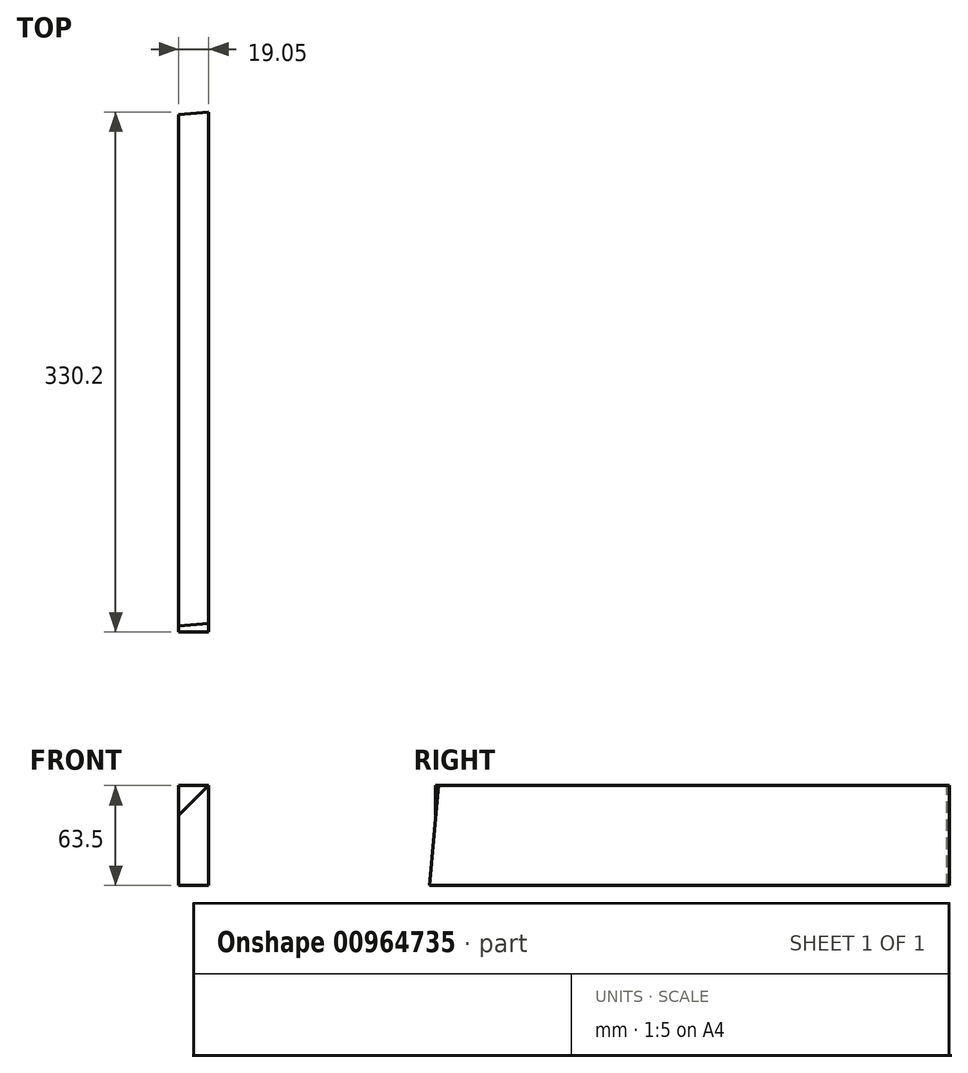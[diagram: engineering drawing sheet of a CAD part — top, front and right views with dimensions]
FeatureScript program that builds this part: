
annotation { "Feature Type Name" : "Feature", "Feature Type Description" : "" }
export const myFeature = defineFeature(function(context is Context, id is Id, definition is map)
    precondition{}
    {
        {
            var Q0;
            Q0=qCreatedBy(makeId("Right.planeOp"),FACE);
            var sketch = newSketch(context, id + "F0", { "sketchPlane" : qUnion([Q0])});
            skLineSegment(sketch, "E0.bottom", {"start": v(0, 0) * mm, "end": v(-330.2, 0) * mm});
            skLineSegment(sketch, "E0.top", {"start": v(0, 63.5) * mm, "end": v(-330.2, 63.5) * mm});
            skLineSegment(sketch, "E0.left", {"start": v(0, 0) * mm, "end": v(0, 63.5) * mm});
            skLineSegment(sketch, "E0.right", {"start": v(-330.2, 0) * mm, "end": v(-330.2, 63.5) * mm});
            skSolve(sketch);
        }
        {
            var Q0;
            Q0 = qSketchRegion(id + "F0", true);
            extrude(context, id + "F1", {"entities" : qUnion([Q0]), "depth" : 19.05 * mm, "offsetDistance" : 25.4 * mm});
        }
        {
            var Q0;
            Q0=makeQuery(id+"F1.opExtrude","SWEPT_FACE",FACE,{"disambiguationData":[OSD([sQuery(id+"F0.wireOp",EDGE,"E0.top")])]});
            var sketch = newSketch(context, id + "F2", { "sketchPlane" : qUnion([Q0])});
            skLineSegment(sketch, "E1", {"start": v(19.05, 0) * mm, "end": v(0, -1.67) * mm});
            skLineSegment(sketch, "E2", {"start": v(0, -1.67) * mm, "end": v(0, 0) * mm});
            skLineSegment(sketch, "E3", {"start": v(0, 0) * mm, "end": v(19.05, 0) * mm});
            skSolve(sketch);
        }
        {
            var Q0;
            Q0 = qSketchRegion(id + "F2", true);
            extrude(context, id + "F3", {"entities" : qUnion([Q0]), "operationType" : NewBodyOperationType.REMOVE, "endBound" : BoundingType.THROUGH_ALL, "oppositeDirection" : true, "depth" : 25.4 * mm, "offsetDistance" : 25.4 * mm});
        }
        {
            var Q0;
            Q0=makeQuery(id+"F1.opExtrude","CAP_FACE",FACE,{"disambiguationData":[OSD([sQuery(id+"F0.wireOp",EDGE,"E0.bottom"),sQuery(id+"F0.wireOp",EDGE,"E0.top"),sQuery(id+"F0.wireOp",EDGE,"E0.left"),sQuery(id+"F0.wireOp",EDGE,"E0.right")])],"isStart":false});
            var sketch = newSketch(context, id + "F4", { "sketchPlane" : qUnion([Q0])});
            skLineSegment(sketch, "E4", {"start": v(-330.2, 63.5) * mm, "end": v(-324.64, 63.5) * mm});
            skLineSegment(sketch, "E5", {"start": v(-324.64, 63.5) * mm, "end": v(-330.2, 0) * mm});
            skLineSegment(sketch, "E6", {"start": v(-330.2, 0) * mm, "end": v(-330.2, 63.5) * mm});
            skSolve(sketch);
        }
        {
            var Q0;
            Q0 = qSketchRegion(id + "F4", true);
            extrude(context, id + "F5", {"entities" : qUnion([Q0]), "operationType" : NewBodyOperationType.REMOVE, "endBound" : BoundingType.THROUGH_ALL, "oppositeDirection" : true, "depth" : 25.4 * mm, "offsetDistance" : 25.4 * mm});
        }
        {
            var Q0;
            Q0=makeQuery(id+"F1.opExtrude","SWEPT_FACE",FACE,{"disambiguationData":[OSD([sQuery(id+"F0.wireOp",EDGE,"E0.top")])]});
            var sketch = newSketch(context, id + "F6", { "sketchPlane" : qUnion([Q0])});
            skLineSegment(sketch, "E7", {"start": v(0, -324.64) * mm, "end": v(0, -326.31) * mm});
            skLineSegment(sketch, "E8", {"start": v(0, -326.31) * mm, "end": v(19.05, -324.64) * mm});
            skLineSegment(sketch, "E9", {"start": v(19.05, -324.64) * mm, "end": v(0, -324.64) * mm});
            skSolve(sketch);
        }
        {
            var Q0;
            Q0 = qSketchRegion(id + "F6", true);
            extrude(context, id + "F7", {"entities" : qUnion([Q0]), "operationType" : NewBodyOperationType.ADD, "oppositeDirection" : true, "depth" : 63.5 * mm, "offsetDistance" : 25.4 * mm});
        }
    });
